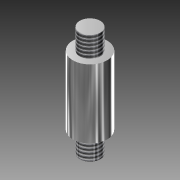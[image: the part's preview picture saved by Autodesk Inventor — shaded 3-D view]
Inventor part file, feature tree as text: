
AUTODESK INVENTOR PART (.ipt)
format: ipt  version: 2015 (Build 190159000, 159)  size: 91,648 bytes
history: native  units: mm
features: extrude x3, sketch x3, thread x2
ambient origin geometry x8: Origin, YZ Plane, XZ Plane, XY Plane, X Axis, Y Axis, Z Axis, Center Point
bodies: Solid1 (feature_tree)
feature tree (8):
  extrude  "Extrusion1"  Depth=10.0mm TaperAngle=0.0deg
  extrude  "Extrusion2"  Depth=3.0mm TaperAngle=0.0deg
  thread  "Thread1"  [1 undecoded]
  extrude  "Extrusion3"  Depth=3.0mm TaperAngle=0.0deg
  thread  "Thread2"  [1 undecoded]
  sketch  "Sketch1"  dims[d0=5.0mm d1=10.0mm d2=0.0mm]
  sketch  "Sketch2"  dims[d3=3.0mm d4=3.0mm d5=0.0mm d6=10.0mm d7=0.0mm]
  sketch  "Sketch3"  dims[d8=3.0mm d9=3.0mm d10=0.0mm d11=10.0mm d12=0.0mm]
note: 2 required parameter values undecoded (feature->parameter linkage not recoverable at this tier; creation-order binding heuristic only, values carry confidence <= 0.55)
